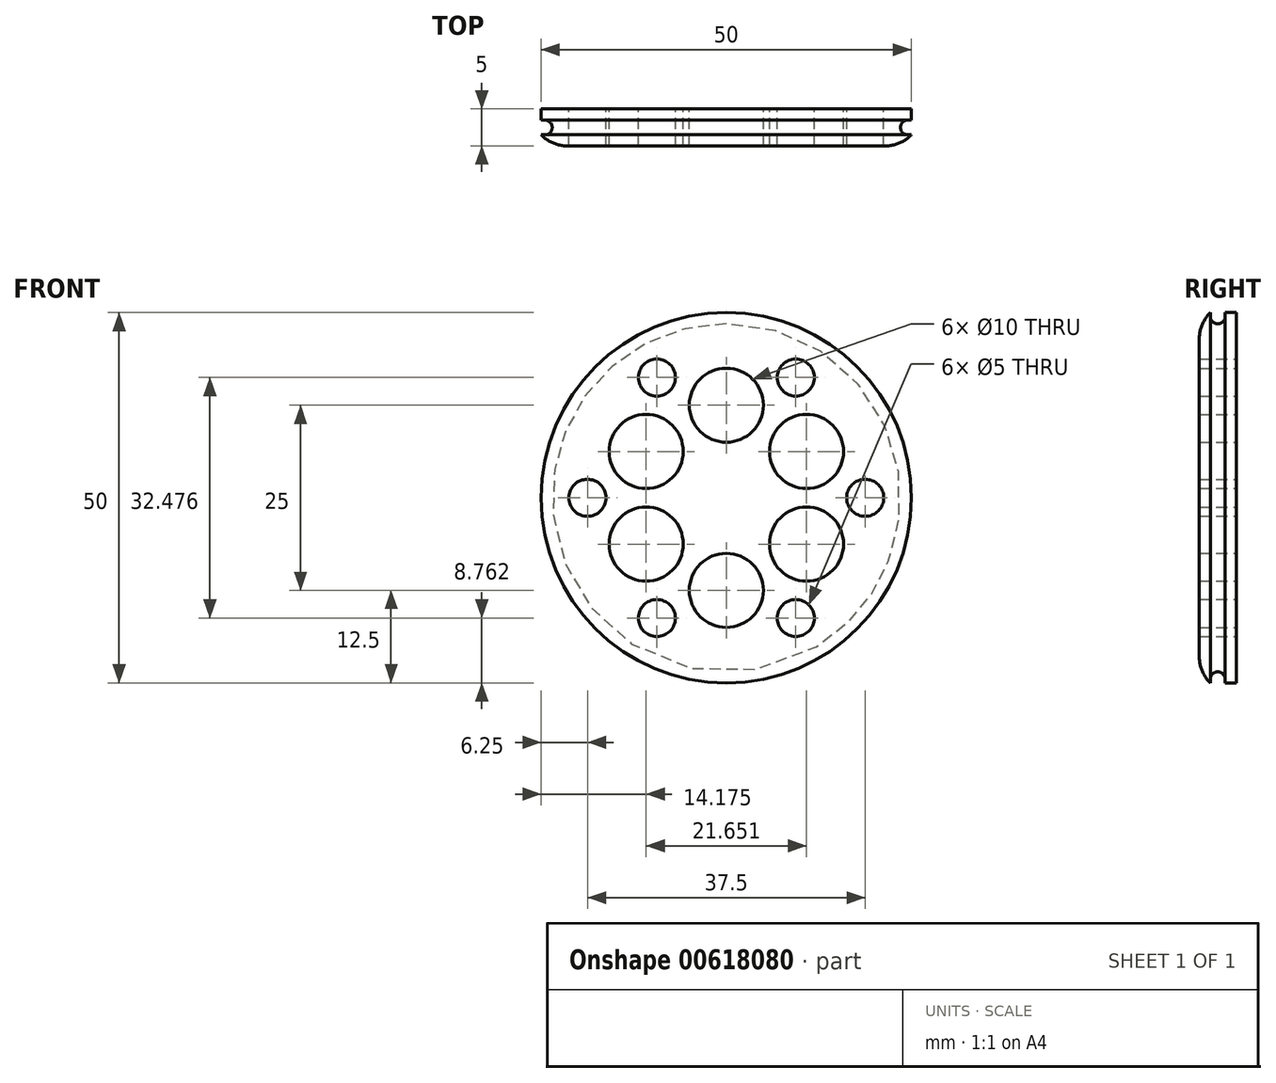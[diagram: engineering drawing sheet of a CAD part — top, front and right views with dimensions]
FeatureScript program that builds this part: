
annotation { "Feature Type Name" : "Feature", "Feature Type Description" : "" }
export const myFeature = defineFeature(function(context is Context, id is Id, definition is map)
    precondition{}
    {
        {
            var Q0;
            Q0=qCreatedBy(makeId("Front.planeOp"),FACE);
            var sketch = newSketch(context, id + "F0", { "sketchPlane" : qUnion([Q0])});
            skCircle(sketch, "E0", {"center": v(0, 0) * mm, "radius": 25 * mm});
            skCircle(sketch, "E1", {"center": v(0, 0) * mm, "radius": 12.5 * mm, "construction": true});
            skCircle(sketch, "E2.cCircle", {"center": v(0, 0) * mm, "radius": 25 * mm, "construction": true});
            skLineSegment(sketch, "E2.0", {"start": v(0, 25) * mm, "end": v(21.65, 12.5) * mm, "construction": true});
            skLineSegment(sketch, "E2.1", {"start": v(21.65, 12.5) * mm, "end": v(21.65, -12.5) * mm, "construction": true});
            skLineSegment(sketch, "E2.2", {"start": v(21.65, -12.5) * mm, "end": v(0, -25) * mm, "construction": true});
            skLineSegment(sketch, "E2.3", {"start": v(0, -25) * mm, "end": v(-21.65, -12.5) * mm, "construction": true});
            skLineSegment(sketch, "E2.4", {"start": v(-21.65, -12.5) * mm, "end": v(-21.65, 12.5) * mm, "construction": true});
            skLineSegment(sketch, "E2.5", {"start": v(-21.65, 12.5) * mm, "end": v(0, 25) * mm, "construction": true});
            skLineSegment(sketch, "E3", {"start": v(-21.65, 12.5) * mm, "end": v(0, 0) * mm, "construction": true});
            skLineSegment(sketch, "E4", {"start": v(0, 25) * mm, "end": v(0, 0) * mm, "construction": true});
            skLineSegment(sketch, "E5", {"start": v(0, 0) * mm, "end": v(-21.65, -12.5) * mm, "construction": true});
            skLineSegment(sketch, "E6", {"start": v(0, -25) * mm, "end": v(0, 0) * mm, "construction": true});
            skLineSegment(sketch, "E7", {"start": v(0, 0) * mm, "end": v(25, 0) * mm, "construction": true});
            skPoint(sketch, "E7.endSnap0", {"position": v(21.65, 0) * mm});
            skLineSegment(sketch, "E8", {"start": v(21.65, 12.5) * mm, "end": v(0, 0) * mm, "construction": true});
            skLineSegment(sketch, "E9", {"start": v(0, 0) * mm, "end": v(21.65, -12.5) * mm, "construction": true});
            skCircle(sketch, "E10", {"center": v(-10.83, 6.25) * mm, "radius": 5 * mm});
            skCircle(sketch, "E11", {"center": v(0, 12.5) * mm, "radius": 5 * mm});
            skCircle(sketch, "E12", {"center": v(10.83, 6.25) * mm, "radius": 5 * mm});
            skCircle(sketch, "E13", {"center": v(10.83, -6.25) * mm, "radius": 5 * mm});
            skCircle(sketch, "E14", {"center": v(0, -12.5) * mm, "radius": 5 * mm});
            skCircle(sketch, "E15", {"center": v(-10.83, -6.25) * mm, "radius": 5 * mm});
            skCircle(sketch, "E16", {"center": v(0, 0) * mm, "radius": 18.75 * mm, "construction": true});
            skLineSegment(sketch, "E17.0", {"start": v(18.75, 0) * mm, "end": v(9.38, -16.24) * mm, "construction": true});
            skLineSegment(sketch, "E17.1", {"start": v(9.38, -16.24) * mm, "end": v(-9.37, -16.24) * mm, "construction": true});
            skLineSegment(sketch, "E17.2", {"start": v(-9.37, -16.24) * mm, "end": v(-18.75, 0) * mm, "construction": true});
            skLineSegment(sketch, "E17.3", {"start": v(-18.75, 0) * mm, "end": v(-9.38, 16.24) * mm, "construction": true});
            skLineSegment(sketch, "E17.4", {"start": v(-9.38, 16.24) * mm, "end": v(9.37, 16.24) * mm, "construction": true});
            skLineSegment(sketch, "E17.5", {"start": v(9.37, 16.24) * mm, "end": v(18.75, 0) * mm, "construction": true});
            skCircle(sketch, "E18", {"center": v(-9.38, 16.24) * mm, "radius": 2.5 * mm});
            skCircle(sketch, "E19", {"center": v(9.37, 16.24) * mm, "radius": 2.5 * mm});
            skCircle(sketch, "E20", {"center": v(18.75, 0) * mm, "radius": 2.5 * mm});
            skCircle(sketch, "E21", {"center": v(9.38, -16.24) * mm, "radius": 2.5 * mm});
            skCircle(sketch, "E22", {"center": v(-9.37, -16.24) * mm, "radius": 2.5 * mm});
            skCircle(sketch, "E23", {"center": v(-18.75, 0) * mm, "radius": 2.5 * mm});
            skSolve(sketch);
        }
        {
            var Q0;
            Q0=makeQuery(id+"F0.imprint","IMPRINT",FACE,{"disambiguationData":[TD([[makeQuery(id+"F0.imprint","IMPRINT",EDGE,{"derivedFrom":sQuery(id+"F0.wireOp",EDGE,"E0")}),1.0]])]});
            extrude(context, id + "F1", {"entities" : qUnion([Q0]), "depth" : 5 * mm, "offsetDistance" : 25 * mm});
        }
        {
            var Q0;
            Q0=makeQuery(id+"F1.opExtrude","CAP_FACE",FACE,{"disambiguationData":[OSD([sQuery(id+"F0.wireOp",EDGE,"E0"),sQuery(id+"F0.wireOp",EDGE,"E10"),sQuery(id+"F0.wireOp",EDGE,"E11"),sQuery(id+"F0.wireOp",EDGE,"E12"),sQuery(id+"F0.wireOp",EDGE,"E13"),sQuery(id+"F0.wireOp",EDGE,"E14"),sQuery(id+"F0.wireOp",EDGE,"E15"),sQuery(id+"F0.wireOp",EDGE,"E18"),sQuery(id+"F0.wireOp",EDGE,"E19"),sQuery(id+"F0.wireOp",EDGE,"E20"),sQuery(id+"F0.wireOp",EDGE,"E21"),sQuery(id+"F0.wireOp",EDGE,"E22"),sQuery(id+"F0.wireOp",EDGE,"E23")])],"isStart":false});
            cPlane(context, id + "F2", {"entities" : qUnion([Q0]), "cplaneType" : CPlaneType.OFFSET, "offset" : 2.5 * mm, "oppositeDirection" : true, "width" : 150 * mm, "height" : 150 * mm});
        }
        {
            var Q0;
            Q0=qCreatedBy(makeId("Right.planeOp"),FACE);
            var sketch = newSketch(context, id + "F3", { "sketchPlane" : qUnion([Q0])});
            skLineSegment(sketch, "E24", {"start": v(0, 0) * mm, "end": v(0, 25) * mm, "construction": true});
            skLineSegment(sketch, "E25", {"start": v(0, 25) * mm, "end": v(-5, 25) * mm, "construction": true});
            skLineSegment(sketch, "E26", {"start": v(0, 25) * mm, "end": v(-1.5, 25) * mm, "construction": true});
            skLineSegment(sketch, "E27", {"start": v(-1.63, 25) * mm, "end": v(-2, 25) * mm, "construction": true});
            skLineSegment(sketch, "E28.left", {"start": v(-3.5, 23.5) * mm, "end": v(-3.5, 25) * mm});
            skLineSegment(sketch, "E28.right", {"start": v(-1.5, 23.5) * mm, "end": v(-1.5, 25) * mm});
            skLineSegment(sketch, "E29", {"start": v(-3.5, 23.5) * mm, "end": v(-1.5, 25.5) * mm, "construction": true});
            skLineSegment(sketch, "E30", {"start": v(-1.5, 23.5) * mm, "end": v(-3.5, 25.5) * mm, "construction": true});
            skCircle(sketch, "E31", {"center": v(-2.5, 24.5) * mm, "radius": 1 * mm});
            skLineSegment(sketch, "E32", {"start": v(-3.5, 25) * mm, "end": v(-3.5, 23.5) * mm});
            skLineSegment(sketch, "E33", {"start": v(-3.5, 25) * mm, "end": v(-1.5, 25) * mm});
            skLineSegment(sketch, "E34", {"start": v(-3.5, 23.5) * mm, "end": v(-3.5, 25.5) * mm});
            skLineSegment(sketch, "E35.trimOffspring", {"start": v(-3, 25) * mm, "end": v(-3.5, 25) * mm, "construction": true});
            skSolve(sketch);
        }
        {
            var Q0;
            Q0=qCreatedBy(makeId("Top.planeOp"),FACE);
            var sketch = newSketch(context, id + "F4", { "sketchPlane" : qUnion([Q0])});
            skLineSegment(sketch, "E36", {"start": v(0, 0) * mm, "end": v(0, -5) * mm, "construction": true});
            skSolve(sketch);
        }
        {
            var Q0;
            Q0 = qSketchRegion(id + "F3", true);
            var Q1;
            Q1=sQuery(id+"F4.wireOp",EDGE,"E36");
            revolve(context, id + "F5", {"operationType" : NewBodyOperationType.REMOVE, "entities" : qUnion([Q0]), "axis" : qUnion([Q1]), "revolveType" : RevolveType.FULL});
        }
        {
            var Q0;
            Q0=makeQuery(id+"F1.opExtrude","CAP_EDGE",EDGE,{"disambiguationData":[OSD([sQuery(id+"F0.wireOp",EDGE,"E0")])],"isStart":false});
            fillet(context, id + "F6", {"entities" : qUnion([Q0]), "radius" : 5 * mm, "tangentPropagation" : true, "allowEdgeOverflow" : false});
        }
    });
